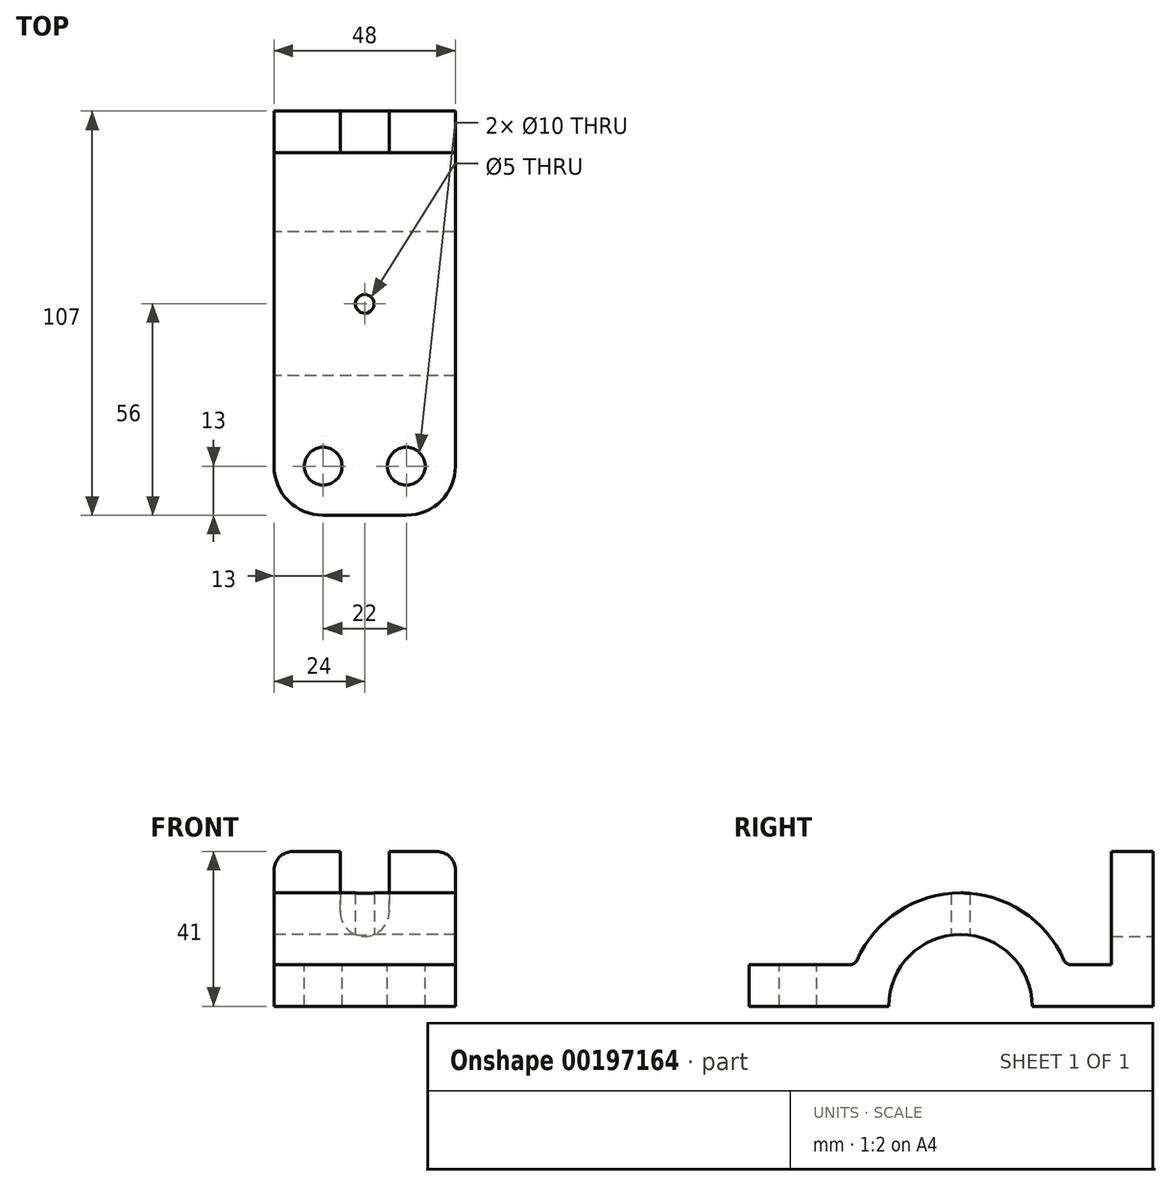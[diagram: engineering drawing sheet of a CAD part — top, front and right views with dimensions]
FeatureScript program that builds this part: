
annotation { "Feature Type Name" : "Feature", "Feature Type Description" : "" }
export const myFeature = defineFeature(function(context is Context, id is Id, definition is map)
    precondition{}
    {
        {
            var Q0;
            Q0=qCreatedBy(makeId("Right.planeOp"),FACE);
            var sketch = newSketch(context, id + "F0", { "sketchPlane" : qUnion([Q0])});
            skLineSegment(sketch, "E0", {"start": v(0, 0) * mm, "end": v(-32, 0) * mm});
            skLineSegment(sketch, "E1", {"start": v(-107, 0) * mm, "end": v(-107, 11) * mm});
            skLineSegment(sketch, "E2", {"start": v(-107, 11) * mm, "end": v(-78.91, 11) * mm});
            skLineSegment(sketch, "E3", {"start": v(-11, 11) * mm, "end": v(-11, 41) * mm});
            skLineSegment(sketch, "E4", {"start": v(-11, 41) * mm, "end": v(0, 41) * mm});
            skLineSegment(sketch, "E5", {"start": v(0, 41) * mm, "end": v(0, 0) * mm});
            skArc(sketch, "E6", {"start": v(-32, 0) * mm, "mid": v(-51, 19) * mm, "end": v(-70, 0) * mm});
            skArc(sketch, "E7", {"start": v(-78.91, 11) * mm, "mid": v(-51, 30) * mm, "end": v(-23.09, 11) * mm});
            skLineSegment(sketch, "E8.trimOffspring", {"start": v(-23.09, 11) * mm, "end": v(-11, 11) * mm});
            skLineSegment(sketch, "E9.trimOffspring", {"start": v(-70, 0) * mm, "end": v(-107, 0) * mm});
            skSolve(sketch);
        }
        {
            var Q0;
            Q0=makeQuery(id+"F0.imprint","IMPRINT",FACE,{"disambiguationData":[TD([[makeQuery(id+"F0.imprint","IMPRINT",EDGE,{"derivedFrom":sQuery(id+"F0.wireOp",EDGE,"E0")}),-1.0]])]});
            extrude(context, id + "F1", {"entities" : qUnion([Q0]), "endBound" : BoundingType.SYMMETRIC, "depth" : 48 * mm});
        }
        {
            var Q0;
            Q0=makeQuery(id+"F1.opExtrude","SWEPT_FACE",FACE,{"disambiguationData":[OSD([sQuery(id+"F0.wireOp",EDGE,"E5")])]});
            var sketch = newSketch(context, id + "F2", { "sketchPlane" : qUnion([Q0])});
            skLineSegment(sketch, "E10.left", {"start": v(6.5, 25) * mm, "end": v(6.5, 41) * mm});
            skLineSegment(sketch, "E10.right", {"start": v(-6.5, 25) * mm, "end": v(-6.5, 41) * mm});
            skPoint(sketch, "E10.middle", {"position": v(0, 41) * mm});
            skArc(sketch, "E11", {"start": v(-6.5, 25) * mm, "mid": v(0, 18.5) * mm, "end": v(6.5, 25) * mm});
            skPoint(sketch, "E12", {"position": v(6.5, 41) * mm});
            skPoint(sketch, "E13", {"position": v(-6.5, 41) * mm});
            skSolve(sketch);
        }
        {
            var Q0;
            {var subQ0=sQuery(id+"F2.wireOp",EDGE,"E10.left");Q0=makeQuery(id+"F2.imprint","IMPRINT",FACE,{"disambiguationData":[TD([[makeQuery(id+"F2.imprint","IMPRINT",EDGE,{"derivedFrom":subQ0}),1.0]])]});}
            extrude(context, id + "F3", {"entities" : qUnion([Q0]), "operationType" : NewBodyOperationType.REMOVE, "oppositeDirection" : true, "depth" : 20.5 * mm});
        }
        {
            var Q0;
            Q0=makeQuery(id+"F1.opExtrude","CAP_EDGE",EDGE,{"disambiguationData":[OSD([sQuery(id+"F0.wireOp",EDGE,"E4")])],"isStart":true});
            var Q1;
            Q1=makeQuery(id+"F1.opExtrude","CAP_EDGE",EDGE,{"disambiguationData":[OSD([sQuery(id+"F0.wireOp",EDGE,"E4")])],"isStart":false});
            fillet(context, id + "F4", {"entities" : qUnion([Q0, Q1]), "radius" : 5 * mm, "tangentPropagation" : true, "allowEdgeOverflow" : false});
        }
        {
            var Q0;
            Q0=makeQuery(id+"F1.opExtrude","CAP_EDGE",EDGE,{"disambiguationData":[OSD([sQuery(id+"F0.wireOp",EDGE,"E1")])],"isStart":true});
            var Q1;
            Q1=makeQuery(id+"F1.opExtrude","CAP_EDGE",EDGE,{"disambiguationData":[OSD([sQuery(id+"F0.wireOp",EDGE,"E1")])],"isStart":false});
            fillet(context, id + "F5", {"entities" : qUnion([Q0, Q1]), "radius" : 13 * mm, "tangentPropagation" : true, "allowEdgeOverflow" : false});
        }
        {
            var Q0;
            Q0=makeQuery(id+"F1.opExtrude","SWEPT_FACE",FACE,{"disambiguationData":[OSD([sQuery(id+"F0.wireOp",EDGE,"E2")])]});
            var sketch = newSketch(context, id + "F6", { "sketchPlane" : qUnion([Q0])});
            skCircle(sketch, "E14", {"center": v(-11, -94) * mm, "radius": 5 * mm});
            skCircle(sketch, "E15", {"center": v(11, -94) * mm, "radius": 5 * mm});
            skSolve(sketch);
        }
        {
            var Q0;
            Q0=makeQuery(id+"F6.imprint","IMPRINT",FACE,{"disambiguationData":[TD([[makeQuery(id+"F6.imprint","IMPRINT",EDGE,{"derivedFrom":sQuery(id+"F6.wireOp",EDGE,"E14")}),1.0]])]});
            var Q1;
            Q1=makeQuery(id+"F6.imprint","IMPRINT",FACE,{"disambiguationData":[TD([[makeQuery(id+"F6.imprint","IMPRINT",EDGE,{"derivedFrom":sQuery(id+"F6.wireOp",EDGE,"E15")}),1.0]])]});
            extrude(context, id + "F7", {"entities" : qUnion([Q0, Q1]), "operationType" : NewBodyOperationType.REMOVE, "oppositeDirection" : true, "depth" : 25 * mm});
        }
        {
            var Q0;
            Q0=qCreatedBy(makeId("Top.planeOp"),FACE);
            var sketch = newSketch(context, id + "F8", { "sketchPlane" : qUnion([Q0])});
            skLineSegment(sketch, "E16.0.0", {"start": v(-24, -70) * mm, "end": v(-24, -32) * mm});
            skLineSegment(sketch, "E16.0.1", {"start": v(-24, -32) * mm, "end": v(24, -32) * mm});
            skLineSegment(sketch, "E16.0.2", {"start": v(24, -32) * mm, "end": v(24, -70) * mm});
            skLineSegment(sketch, "E16.0.3", {"start": v(24, -70) * mm, "end": v(-24, -70) * mm});
            skCircle(sketch, "E17", {"center": v(0, -51) * mm, "radius": 2.5 * mm});
            skPoint(sketch, "E17.centerSnap0", {"position": v(-24, -51) * mm});
            skPoint(sketch, "E17.centerSnap1", {"position": v(0, -70) * mm});
            skSolve(sketch);
        }
        {
            var Q0;
            Q0=makeQuery(id+"F8.imprint","IMPRINT",FACE,{"disambiguationData":[TD([[makeQuery(id+"F8.imprint","IMPRINT",EDGE,{"derivedFrom":sQuery(id+"F8.wireOp",EDGE,"E17")}),1.0]])]});
            extrude(context, id + "F9", {"entities" : qUnion([Q0]), "operationType" : NewBodyOperationType.REMOVE, "depth" : 38.6 * mm});
        }
        {
            var Q0;
            Q0=makeQuery(id+"F1.opExtrude","SWEPT_EDGE",EDGE,{"disambiguationData":[OSD([sQuery(id+"F0.wireOp",EDGE,"E2"),sQuery(id+"F0.wireOp",EDGE,"E7")])]});
            var Q1;
            Q1=makeQuery(id+"F1.opExtrude","SWEPT_EDGE",EDGE,{"disambiguationData":[OSD([sQuery(id+"F0.wireOp",EDGE,"E7"),sQuery(id+"F0.wireOp",EDGE,"E8.trimOffspring")])]});
            fillet(context, id + "F10", {"entities" : qUnion([Q0, Q1]), "radius" : 2 * mm, "tangentPropagation" : true, "allowEdgeOverflow" : false});
        }
    });
